# Revit family: GD1 Square Poseur Height
name_source: partatom
category: Furniture
revit_build: Autodesk Revit 2016 (Build: 20160525_1230(x64)
units: mm (PartAtom-declared; Revit-internal decimal feet)

## family parameters
Always vertical = Yes
Cut with Voids When Loaded = No
OmniClass Number = 23.40.20.00
OmniClass Title = General Furniture and Specialties
Room Calculation Point = No
Shared = No
Work Plane-Based = No

## types (6) — shared parameters
Assembly Code = E2020200
Frame = Gresham - Black Metal
Manufacturer = Gresham Office Furniture
Range = GD1
Table Top = Gresham - White MFC
URL = www.gof.co.uk

## per-type parameters (varying)
| type | Power Module | Product Code | Width |
| 1600 x 1600 | No | GD1D2 | 1600 mm  [stored 5.24934 ft] |
| 1200 x 1200 | No | GD1E2 | 1200 mm |
| 1000 x 1000 | No | GD1F2 | 1000 mm  [stored 3.28084 ft] |
| 1600 x 1600 C/W Power | Yes | GD1D4 | 1600 mm  [stored 5.24934 ft] |
| 1200 x 1200 C/W Power | Yes | GD1E4 | 1200 mm |
| 1000 x 1000 C/W Power | Yes | GD1F4 | 1000 mm  [stored 3.28084 ft] |

note: [stored X ft] marks values corroborated as IEEE doubles in the binary element streams (Revit-internal decimal feet)

## geometry (parser evidence)
native form markers: Sweep x9
no freeform markers — native parametric forms only
